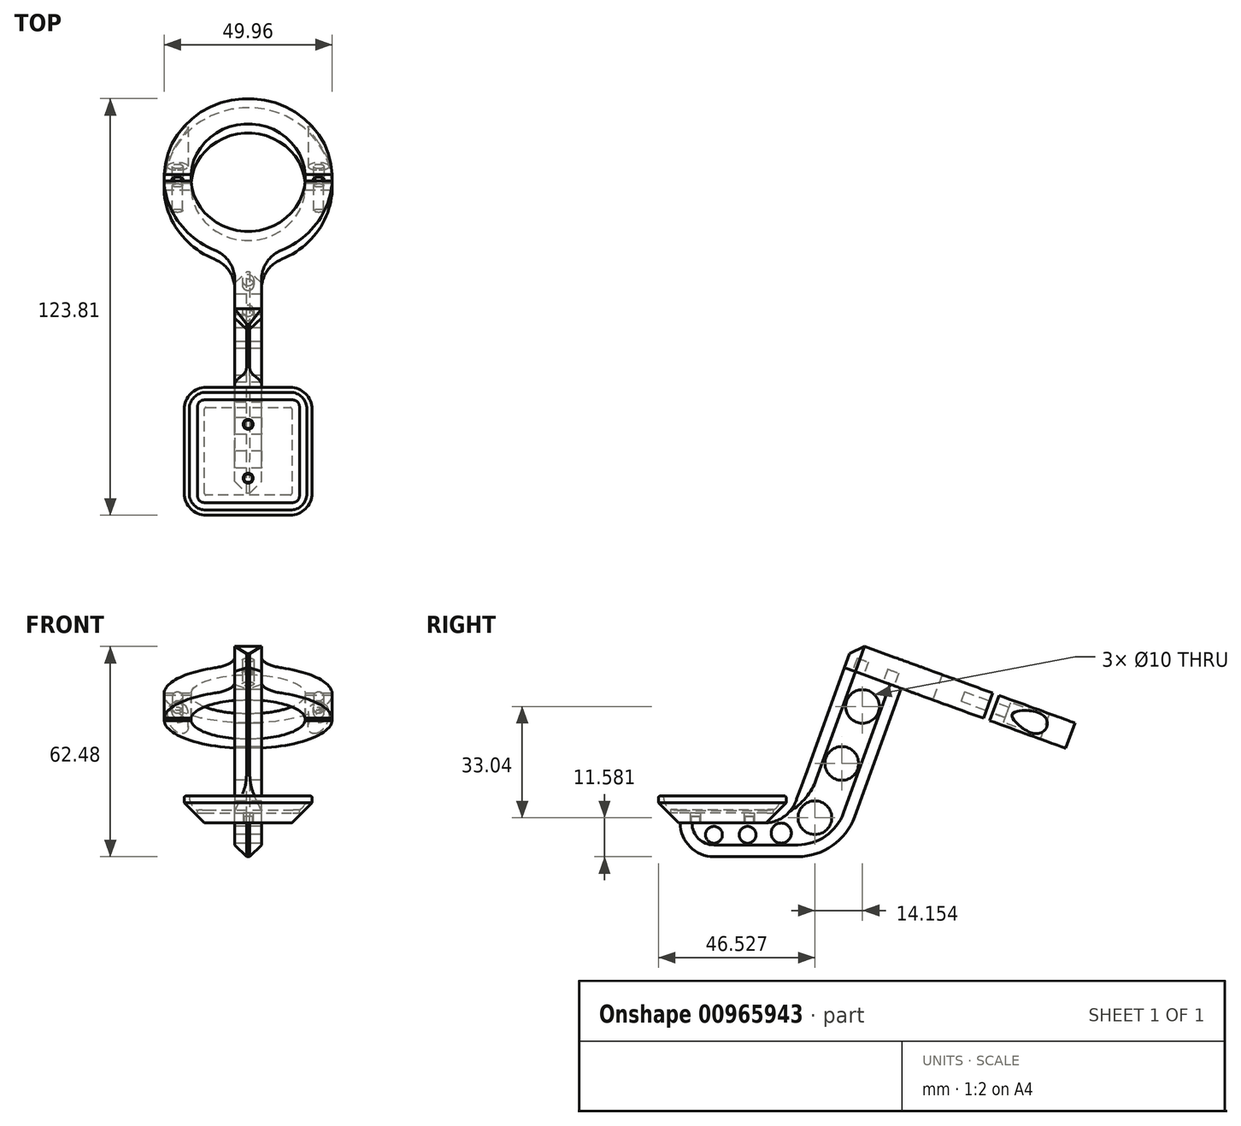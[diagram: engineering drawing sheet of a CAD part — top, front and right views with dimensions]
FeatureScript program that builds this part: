
annotation { "Feature Type Name" : "Feature", "Feature Type Description" : "" }
export const myFeature = defineFeature(function(context is Context, id is Id, definition is map)
    precondition{}
    {
        {
            var Q0;
            Q0=qCreatedBy(makeId("Top.planeOp"),FACE);
            var sketch = newSketch(context, id + "F0", { "sketchPlane" : qUnion([Q0])});
            skLineSegment(sketch, "E0.bottom", {"start": v(-19, 19) * mm, "end": v(19, 19) * mm});
            skLineSegment(sketch, "E0.top", {"start": v(-19, -19) * mm, "end": v(19, -19) * mm});
            skLineSegment(sketch, "E0.left", {"start": v(-19, 19) * mm, "end": v(-19, -19) * mm});
            skLineSegment(sketch, "E0.right", {"start": v(19, 19) * mm, "end": v(19, -19) * mm});
            skSolve(sketch);
        }
        {
            var Q0;
            Q0 = qSketchRegion(id + "F0", true);
            extrude(context, id + "F1", {"entities" : qUnion([Q0]), "depth" : 8 * mm, "offsetDistance" : 25 * mm});
        }
        {
            var Q0;
            Q0=makeQuery(id+"F1.opExtrude","SWEPT_EDGE",EDGE,{"disambiguationData":[OSD([sQuery(id+"F0.wireOp",EDGE,"E0.top"),sQuery(id+"F0.wireOp",EDGE,"E0.left")])]});
            var Q1;
            Q1=makeQuery(id+"F1.opExtrude","SWEPT_EDGE",EDGE,{"disambiguationData":[OSD([sQuery(id+"F0.wireOp",EDGE,"E0.top"),sQuery(id+"F0.wireOp",EDGE,"E0.right")])]});
            var Q2;
            Q2=makeQuery(id+"F1.opExtrude","SWEPT_EDGE",EDGE,{"disambiguationData":[OSD([sQuery(id+"F0.wireOp",EDGE,"E0.bottom"),sQuery(id+"F0.wireOp",EDGE,"E0.right")])]});
            var Q3;
            Q3=makeQuery(id+"F1.opExtrude","SWEPT_EDGE",EDGE,{"disambiguationData":[OSD([sQuery(id+"F0.wireOp",EDGE,"E0.bottom"),sQuery(id+"F0.wireOp",EDGE,"E0.left")])]});
            fillet(context, id + "F2", {"entities" : qUnion([Q0, Q1, Q2, Q3]), "radius" : 6.5 * mm, "tangentPropagation" : true, "allowEdgeOverflow" : false});
        }
        {
            var Q0;
            Q0=makeQuery(id+"F1.opExtrude","CAP_FACE",FACE,{"disambiguationData":[OSD([sQuery(id+"F0.wireOp",EDGE,"E0.bottom"),sQuery(id+"F0.wireOp",EDGE,"E0.top"),sQuery(id+"F0.wireOp",EDGE,"E0.left"),sQuery(id+"F0.wireOp",EDGE,"E0.right")])],"isStart":false});
            var sketch = newSketch(context, id + "F3", { "sketchPlane" : qUnion([Q0])});
            skLineSegment(sketch, "E1.bottom", {"start": v(-17.5, 17.5) * mm, "end": v(17.5, 17.5) * mm});
            skLineSegment(sketch, "E1.top", {"start": v(-17.5, -17.5) * mm, "end": v(17.5, -17.5) * mm});
            skLineSegment(sketch, "E1.left", {"start": v(-17.5, 17.5) * mm, "end": v(-17.5, -17.5) * mm});
            skLineSegment(sketch, "E1.right", {"start": v(17.5, 17.5) * mm, "end": v(17.5, -17.5) * mm});
            skSolve(sketch);
        }
        {
            var Q0;
            Q0 = qSketchRegion(id + "F3", true);
            extrude(context, id + "F4", {"entities" : qUnion([Q0]), "oppositeDirection" : true, "depth" : 5 * mm, "offsetDistance" : 25 * mm});
        }
        {
            var Q0;
            Q0=makeQuery(id+"F4.opExtrude","SWEPT_EDGE",EDGE,{"disambiguationData":[OSD([sQuery(id+"F3.wireOp",EDGE,"E1.top"),sQuery(id+"F3.wireOp",EDGE,"E1.left")])]});
            var Q1;
            Q1=makeQuery(id+"F4.opExtrude","SWEPT_EDGE",EDGE,{"disambiguationData":[OSD([sQuery(id+"F3.wireOp",EDGE,"E1.bottom"),sQuery(id+"F3.wireOp",EDGE,"E1.left")])]});
            var Q2;
            Q2=makeQuery(id+"F4.opExtrude","SWEPT_EDGE",EDGE,{"disambiguationData":[OSD([sQuery(id+"F3.wireOp",EDGE,"E1.bottom"),sQuery(id+"F3.wireOp",EDGE,"E1.right")])]});
            var Q3;
            Q3=makeQuery(id+"F4.opExtrude","SWEPT_EDGE",EDGE,{"disambiguationData":[OSD([sQuery(id+"F3.wireOp",EDGE,"E1.top"),sQuery(id+"F3.wireOp",EDGE,"E1.right")])]});
            fillet(context, id + "F5", {"entities" : qUnion([Q0, Q1, Q2, Q3]), "radius" : 5 * mm, "tangentPropagation" : true, "allowEdgeOverflow" : false});
        }
        {
            var Q0;
            Q0=makeQuery(id+"F4.opExtrude","CAP_EDGE",EDGE,{"disambiguationData":[OSD([sQuery(id+"F3.wireOp",EDGE,"E1.right")])],"isStart":false});
            fillet(context, id + "F6", {"entities" : qUnion([Q0]), "radius" : 5 * mm, "tangentPropagation" : true, "allowEdgeOverflow" : false});
        }
        {
            var Q0;
            Q0=makeQuery(id+"F4.opExtrude","SWEPT_BODY",BODY,{"disambiguationData":[OSD([sQuery(id+"F3.wireOp",EDGE,"E1.bottom"),sQuery(id+"F3.wireOp",EDGE,"E1.top"),sQuery(id+"F3.wireOp",EDGE,"E1.left"),sQuery(id+"F3.wireOp",EDGE,"E1.right")])]});
            var Q1;
            Q1=makeQuery(id+"F1.opExtrude","SWEPT_BODY",BODY,{"disambiguationData":[OSD([sQuery(id+"F0.wireOp",EDGE,"E0.bottom"),sQuery(id+"F0.wireOp",EDGE,"E0.top"),sQuery(id+"F0.wireOp",EDGE,"E0.left"),sQuery(id+"F0.wireOp",EDGE,"E0.right")])]});
            booleanBodies(context, id + "F7", {"operationType" : BooleanOperationType.SUBTRACTION, "tools" : qUnion([Q0]), "targets" : qUnion([Q1])});
        }
        {
            var Q0;
            Q0=makeQuery(id+"F1.opExtrude","CAP_FACE",FACE,{"disambiguationData":[OSD([sQuery(id+"F0.wireOp",EDGE,"E0.bottom"),sQuery(id+"F0.wireOp",EDGE,"E0.top"),sQuery(id+"F0.wireOp",EDGE,"E0.left"),sQuery(id+"F0.wireOp",EDGE,"E0.right")])],"isStart":false});
            var sketch = newSketch(context, id + "F8", { "sketchPlane" : qUnion([Q0])});
            skLineSegment(sketch, "E2.bottom", {"start": v(-15.05, 15.25) * mm, "end": v(15.25, 15.25) * mm});
            skLineSegment(sketch, "E2.top", {"start": v(-15.05, -15.25) * mm, "end": v(15.25, -15.25) * mm});
            skLineSegment(sketch, "E2.left", {"start": v(-15.05, 15.25) * mm, "end": v(-15.05, -15.25) * mm});
            skLineSegment(sketch, "E2.right", {"start": v(15.25, 15.25) * mm, "end": v(15.25, -15.25) * mm});
            skSolve(sketch);
        }
        {
            var Q0;
            Q0 = qSketchRegion(id + "F8", true);
            extrude(context, id + "F9", {"entities" : qUnion([Q0]), "oppositeDirection" : true, "depth" : 5 * mm, "offsetDistance" : 25 * mm});
        }
        {
            var Q0;
            Q0=makeQuery(id+"F1.opExtrude","CAP_EDGE",EDGE,{"disambiguationData":[OSD([sQuery(id+"F0.wireOp",EDGE,"E0.top")])],"isStart":false});
            var Q1;
            {var subQ0=sQuery(id+"F3.wireOp",EDGE,"E1.top");Q1=makeQuery(id+"F7.opBoolean","COPY",EDGE,{"derivedFrom":makeQuery(id+"F6.opFillet","BLEND_EDGE",EDGE,{"blendedFrom":[makeQuery(id+"F4.opExtrude","CAP_EDGE",EDGE,{"disambiguationData":[OSD([subQ0])],"isStart":false}),makeQuery(id+"F4.opExtrude","CAP_FACE",FACE,{"disambiguationData":[OSD([sQuery(id+"F3.wireOp",EDGE,"E1.bottom"),subQ0,sQuery(id+"F3.wireOp",EDGE,"E1.left"),sQuery(id+"F3.wireOp",EDGE,"E1.right")])],"isStart":true})],"blendedInto":[makeQuery(id+"F4.opExtrude","CAP_FACE",FACE,{"disambiguationData":[OSD([sQuery(id+"F3.wireOp",EDGE,"E1.bottom"),subQ0,sQuery(id+"F3.wireOp",EDGE,"E1.left"),sQuery(id+"F3.wireOp",EDGE,"E1.right")])],"isStart":true})]})});}
            fillet(context, id + "F10", {"entities" : qUnion([Q0, Q1]), "radius" : .5 * mm, "tangentPropagation" : true, "allowEdgeOverflow" : false});
        }
        {
            var Q0;
            Q0=qCreatedBy(makeId("Right.planeOp"),FACE);
            var sketch = newSketch(context, id + "F11", { "sketchPlane" : qUnion([Q0])});
            skLineSegment(sketch, "E3", {"start": v(-12.5, 0) * mm, "end": v(12.5, 0) * mm});
            skLineSegment(sketch, "E4", {"start": v(-12.5, 0) * mm, "end": v(-12.5, 0) * mm});
            skLineSegment(sketch, "E5", {"start": v(-2.5, -10) * mm, "end": v(22.41, -10) * mm});
            skLineSegment(sketch, "E6", {"start": v(39.33, 1.84) * mm, "end": v(53.22, 40) * mm});
            skLineSegment(sketch, "E7", {"start": v(21.9, 6.58) * mm, "end": v(36.3, 46.16) * mm});
            skPoint(sketch, "E8.visualSharp", {"position": v(-12.5, -10) * mm});
            skArc(sketch, "E8.filletArc", {"start": v(-12.5, 0) * mm, "mid": v(-9.57, -7.07) * mm, "end": v(-2.5, -10) * mm});
            skArc(sketch, "E9.filletArc", {"start": v(12.5, 0) * mm, "mid": v(18.24, 1.8) * mm, "end": v(21.9, 6.58) * mm});
            skPoint(sketch, "E10.visualSharp", {"position": v(35.02, -10) * mm});
            skArc(sketch, "E10.filletArc", {"start": v(22.41, -10) * mm, "mid": v(32.74, -6.74) * mm, "end": v(39.33, 1.84) * mm});
            skPoint(sketch, "E11.orphan", {"position": v(27.55, 55.87) * mm});
            skLineSegment(sketch, "E12", {"start": v(36.3, 46.16) * mm, "end": v(53.22, 40) * mm});
            skCircle(sketch, "E13", {"center": v(41.68, 34.62) * mm, "radius": 5 * mm});
            skCircle(sketch, "E14", {"center": v(35.52, 17.7) * mm, "radius": 5 * mm});
            skPoint(sketch, "E15.orphan", {"position": v(59, 55.87) * mm});
            skCircle(sketch, "E16", {"center": v(27.53, 1.58) * mm, "radius": 5 * mm});
            skCircle(sketch, "E17", {"center": v(17.53, -3) * mm, "radius": 3 * mm});
            skCircle(sketch, "E18", {"center": v(7.53, -3.5) * mm, "radius": 2.5 * mm});
            skCircle(sketch, "E19", {"center": v(-2.47, -3.5) * mm, "radius": 2.5 * mm});
            skSolve(sketch);
        }
        {
            var Q0;
            Q0 = qSketchRegion(id + "F11", true);
            extrude(context, id + "F12", {"entities" : qUnion([Q0]), "depth" : 4 * mm, "offsetDistance" : 25 * mm, "hasSecondDirection" : true, "secondDirectionOppositeDirection" : true, "secondDirectionDepth" : 4 * mm});
        }
        {
            var Q0;
            Q0=makeQuery(id+"F1.opExtrude","CAP_FACE",FACE,{"disambiguationData":[OSD([sQuery(id+"F0.wireOp",EDGE,"E0.bottom"),sQuery(id+"F0.wireOp",EDGE,"E0.top"),sQuery(id+"F0.wireOp",EDGE,"E0.left"),sQuery(id+"F0.wireOp",EDGE,"E0.right")])],"isStart":true});
            var sketch = newSketch(context, id + "F13", { "sketchPlane" : qUnion([Q0])});
            skCircle(sketch, "E20", {"center": v(0, 8) * mm, "radius": 1.5 * mm});
            skCircle(sketch, "E21", {"center": v(0, -8) * mm, "radius": 1.5 * mm});
            skSolve(sketch);
        }
        {
            var Q0;
            Q0 = qSketchRegion(id + "F13", true);
            extrude(context, id + "F14", {"entities" : qUnion([Q0]), "operationType" : NewBodyOperationType.REMOVE, "oppositeDirection" : true, "depth" : 25 * mm, "offsetDistance" : 25 * mm});
        }
        {
            var Q0;
            Q0=makeQuery(id+"F12.opExtrude","SWEPT_FACE",FACE,{"disambiguationData":[OSD([sQuery(id+"F11.wireOp",EDGE,"E3")])]});
            var sketch = newSketch(context, id + "F15", { "sketchPlane" : qUnion([Q0])});
            skCircle(sketch, "E22", {"center": v(0, 8) * mm, "radius": 1.25 * mm});
            skCircle(sketch, "E23", {"center": v(0, -8) * mm, "radius": 1.25 * mm});
            skPoint(sketch, "E23.centerSnap0", {"position": v(0, -12.5) * mm});
            skSolve(sketch);
        }
        {
            var Q0;
            Q0 = qSketchRegion(id + "F15", true);
            extrude(context, id + "F16", {"entities" : qUnion([Q0]), "operationType" : NewBodyOperationType.ADD, "depth" : 2 * mm, "offsetDistance" : 25 * mm});
        }
        {
            var Q0;
            Q0=makeQuery(id+"F12.opExtrude","SWEPT_FACE",FACE,{"disambiguationData":[OSD([sQuery(id+"F11.wireOp",EDGE,"E12")])]});
            var sketch = newSketch(context, id + "F17", { "sketchPlane" : qUnion([Q0])});
            skLineSegment(sketch, "E24", {"start": v(12, 26.33) * mm, "end": v(4, 26.33) * mm});
            skLineSegment(sketch, "E25", {"start": v(4, 26.33) * mm, "end": v(4, 18.33) * mm});
            skLineSegment(sketch, "E26", {"start": v(4, 18.33) * mm, "end": v(-4, 18.33) * mm});
            skLineSegment(sketch, "E27", {"start": v(-4, 18.33) * mm, "end": v(-4, 26.33) * mm});
            skLineSegment(sketch, "E28", {"start": v(-4, 26.33) * mm, "end": v(-12, 26.33) * mm});
            skLineSegment(sketch, "E29", {"start": v(-12, 26.33) * mm, "end": v(-12, 1.33) * mm});
            skLineSegment(sketch, "E30", {"start": v(-12, 1.33) * mm, "end": v(12, 1.33) * mm});
            skLineSegment(sketch, "E31", {"start": v(12, 1.33) * mm, "end": v(12, 26.33) * mm});
            skSolve(sketch);
        }
        {
            var Q0;
            Q0 = qSketchRegion(id + "F17", true);
            extrude(context, id + "F18", {"entities" : qUnion([Q0]), "oppositeDirection" : true, "depth" : 49 * mm, "offsetDistance" : 25 * mm});
        }
        {
            var Q0;
            Q0=makeQuery(id+"F18.opExtrude","CAP_EDGE",EDGE,{"disambiguationData":[OSD([sQuery(id+"F17.wireOp",EDGE,"E26")])],"isStart":false});
            fillet(context, id + "F19", {"entities" : qUnion([Q0]), "radius" : 15 * mm, "tangentPropagation" : true, "allowEdgeOverflow" : false});
        }
        {
            var Q0;
            Q0=makeQuery(id+"F12.opExtrude","SWEPT_FACE",FACE,{"disambiguationData":[OSD([sQuery(id+"F11.wireOp",EDGE,"E12")])]});
            var sketch = newSketch(context, id + "F20", { "sketchPlane" : qUnion([Q0])});
            skCircle(sketch, "E32", {"center": v(0, 22.67) * mm, "radius": 1.5 * mm});
            skCircle(sketch, "E33", {"center": v(0, 32.33) * mm, "radius": 1.5 * mm});
            skSolve(sketch);
        }
        {
            var Q0;
            Q0 = qSketchRegion(id + "F20", true);
            extrude(context, id + "F21", {"entities" : qUnion([Q0]), "operationType" : NewBodyOperationType.ADD, "depth" : 1.7 * mm, "offsetDistance" : 25 * mm});
        }
        {
            var Q0;
            Q0=makeQuery(id+"F9.opExtrude","SWEPT_EDGE",EDGE,{"disambiguationData":[OSD([sQuery(id+"F8.wireOp",EDGE,"E2.top"),sQuery(id+"F8.wireOp",EDGE,"E2.right")])]});
            var Q1;
            Q1=makeQuery(id+"F9.opExtrude","SWEPT_EDGE",EDGE,{"disambiguationData":[OSD([sQuery(id+"F8.wireOp",EDGE,"E2.bottom"),sQuery(id+"F8.wireOp",EDGE,"E2.right")])]});
            var Q2;
            Q2=makeQuery(id+"F9.opExtrude","SWEPT_EDGE",EDGE,{"disambiguationData":[OSD([sQuery(id+"F8.wireOp",EDGE,"E2.top"),sQuery(id+"F8.wireOp",EDGE,"E2.left")])]});
            var Q3;
            Q3=makeQuery(id+"F9.opExtrude","SWEPT_EDGE",EDGE,{"disambiguationData":[OSD([sQuery(id+"F8.wireOp",EDGE,"E2.bottom"),sQuery(id+"F8.wireOp",EDGE,"E2.left")])]});
            fillet(context, id + "F22", {"entities" : qUnion([Q0, Q1, Q2, Q3]), "radius" : 2 * mm, "tangentPropagation" : true, "allowEdgeOverflow" : false});
        }
        {
            var Q0;
            Q0=makeQuery(id+"F9.opExtrude","SWEPT_BODY",BODY,{"disambiguationData":[OSD([sQuery(id+"F8.wireOp",EDGE,"E2.bottom"),sQuery(id+"F8.wireOp",EDGE,"E2.top"),sQuery(id+"F8.wireOp",EDGE,"E2.left"),sQuery(id+"F8.wireOp",EDGE,"E2.right")])]});
            var Q1;
            Q1=makeQuery(id+"F1.opExtrude","SWEPT_BODY",BODY,{"disambiguationData":[OSD([sQuery(id+"F0.wireOp",EDGE,"E0.bottom"),sQuery(id+"F0.wireOp",EDGE,"E0.top"),sQuery(id+"F0.wireOp",EDGE,"E0.left"),sQuery(id+"F0.wireOp",EDGE,"E0.right")])]});
            booleanBodies(context, id + "F23", {"operationType" : BooleanOperationType.SUBTRACTION, "tools" : qUnion([Q0]), "targets" : qUnion([Q1])});
        }
        {
            var Q0;
            Q0=makeQuery(id+"F1.opExtrude","CAP_EDGE",EDGE,{"disambiguationData":[OSD([sQuery(id+"F0.wireOp",EDGE,"E0.top")])],"isStart":true});
            chamfer(context, id + "F24", {"entities" : qUnion([Q0]), "width" : 6 * mm, "tangentPropagation" : true});
        }
        {
            var Q0;
            Q0=makeQuery(id+"F18.opExtrude","SWEPT_EDGE",EDGE,{"disambiguationData":[OSD([sQuery(id+"F17.wireOp",EDGE,"E25"),sQuery(id+"F17.wireOp",EDGE,"E26")])]});
            chamfer(context, id + "F25", {"entities" : qUnion([Q0]), "width" : 3.5 * mm, "tangentPropagation" : true});
        }
        {
            var Q0;
            Q0=makeQuery(id+"F18.opExtrude","SWEPT_EDGE",EDGE,{"disambiguationData":[OSD([sQuery(id+"F17.wireOp",EDGE,"E26"),sQuery(id+"F17.wireOp",EDGE,"E27")])]});
            var Q1;
            Q1=makeQuery(id+"F19.opFillet","BLEND_EDGE",EDGE,{"blendedFrom":[makeQuery(id+"F18.opExtrude","CAP_EDGE",EDGE,{"disambiguationData":[OSD([sQuery(id+"F17.wireOp",EDGE,"E26")])],"isStart":false}),makeQuery(id+"F18.opExtrude","SWEPT_FACE",FACE,{"disambiguationData":[OSD([sQuery(id+"F17.wireOp",EDGE,"E27")])]})],"blendedInto":[makeQuery(id+"F18.opExtrude","SWEPT_FACE",FACE,{"disambiguationData":[OSD([sQuery(id+"F17.wireOp",EDGE,"E27")])]})]});
            chamfer(context, id + "F26", {"entities" : qUnion([Q0, Q1]), "width" : 3.5 * mm, "tangentPropagation" : true});
        }
        {
            var Q0;
            Q0=makeQuery(id+"F18.opExtrude","SWEPT_BODY",BODY,{"disambiguationData":[OSD([sQuery(id+"F17.wireOp",EDGE,"E24"),sQuery(id+"F17.wireOp",EDGE,"E25"),sQuery(id+"F17.wireOp",EDGE,"E26"),sQuery(id+"F17.wireOp",EDGE,"E27"),sQuery(id+"F17.wireOp",EDGE,"E28"),sQuery(id+"F17.wireOp",EDGE,"E29"),sQuery(id+"F17.wireOp",EDGE,"E30"),sQuery(id+"F17.wireOp",EDGE,"E31")])]});
            var Q1;
            Q1=makeQuery(id+"F12.opExtrude","SWEPT_BODY",BODY,{"disambiguationData":[OSD([sQuery(id+"F11.wireOp",EDGE,"E3"),sQuery(id+"F11.wireOp",EDGE,"E5"),sQuery(id+"F11.wireOp",EDGE,"E6"),sQuery(id+"F11.wireOp",EDGE,"E7"),sQuery(id+"F11.wireOp",EDGE,"E8.filletArc"),sQuery(id+"F11.wireOp",EDGE,"E9.filletArc"),sQuery(id+"F11.wireOp",EDGE,"E10.filletArc"),sQuery(id+"F11.wireOp",EDGE,"E12"),sQuery(id+"F11.wireOp",EDGE,"E13"),sQuery(id+"F11.wireOp",EDGE,"E14"),sQuery(id+"F11.wireOp",EDGE,"E16"),sQuery(id+"F11.wireOp",EDGE,"E17"),sQuery(id+"F11.wireOp",EDGE,"E18"),sQuery(id+"F11.wireOp",EDGE,"E19")])]});
            booleanBodies(context, id + "F27", {"operationType" : BooleanOperationType.SUBTRACTION, "tools" : qUnion([Q0]), "targets" : qUnion([Q1])});
        }
        {
            var Q0;
            Q0=makeQuery(id+"F12.opExtrude","CAP_EDGE",EDGE,{"disambiguationData":[OSD([sQuery(id+"F11.wireOp",EDGE,"E8.filletArc")])],"isStart":false});
            chamfer(context, id + "F28", {"entities" : qUnion([Q0]), "width" : 3.5 * mm, "tangentPropagation" : true});
        }
        {
            var Q0;
            Q0=makeQuery(id+"F12.opExtrude","CAP_EDGE",EDGE,{"disambiguationData":[OSD([sQuery(id+"F11.wireOp",EDGE,"E5")])],"isStart":true});
            chamfer(context, id + "F29", {"entities" : qUnion([Q0]), "width" : 3.5 * mm, "tangentPropagation" : true});
        }
        {
            var Q0;
            Q0=makeQuery(id+"F12.opExtrude","SWEPT_FACE",FACE,{"disambiguationData":[OSD([sQuery(id+"F11.wireOp",EDGE,"E12")])]});
            var sketch = newSketch(context, id + "F30", { "sketchPlane" : qUnion([Q0])});
            skArc(sketch, "E34", {"start": v(-16.97, 62.32) * mm, "mid": v(0, 46.32) * mm, "end": v(16.97, 62.32) * mm});
            skArc(sketch, "E35", {"start": v(-24.98, 62.32) * mm, "mid": v(-20.64, 49.21) * mm, "end": v(-10, 40.4) * mm});
            skLineSegment(sketch, "E36", {"start": v(-24.98, 62.32) * mm, "end": v(-16.97, 62.32) * mm});
            skLineSegment(sketch, "E37", {"start": v(16.97, 62.32) * mm, "end": v(24.98, 62.32) * mm});
            skLineSegment(sketch, "E38", {"start": v(4, 21.83) * mm, "end": v(4, 31.24) * mm});
            skLineSegment(sketch, "E39", {"start": v(-4, 21.83) * mm, "end": v(-4, 31.24) * mm});
            skLineSegment(sketch, "E40", {"start": v(4, 21.83) * mm, "end": v(0.5, 18.33) * mm});
            skLineSegment(sketch, "E41", {"start": v(0.5, 18.33) * mm, "end": v(-0.5, 18.33) * mm});
            skLineSegment(sketch, "E42", {"start": v(-0.5, 18.33) * mm, "end": v(-4, 21.83) * mm});
            skArc(sketch, "E43.trimOffspring", {"start": v(10, 40.4) * mm, "mid": v(20.64, 49.21) * mm, "end": v(24.98, 62.32) * mm});
            skArc(sketch, "E44.filletArc", {"start": v(-4, 31.24) * mm, "mid": v(-5.63, 36.72) * mm, "end": v(-10, 40.4) * mm});
            skArc(sketch, "E45.filletArc", {"start": v(10, 40.4) * mm, "mid": v(5.63, 36.72) * mm, "end": v(4, 31.24) * mm});
            skSolve(sketch);
        }
        {
            var Q0;
            Q0 = qSketchRegion(id + "F30", true);
            extrude(context, id + "F31", {"entities" : qUnion([Q0]), "depth" : 8 * mm, "offsetDistance" : 25 * mm});
        }
        {
            var Q0;
            Q0=makeQuery(id+"F31.opExtrude","CAP_EDGE",EDGE,{"disambiguationData":[OSD([sQuery(id+"F30.wireOp",EDGE,"E41")])],"isStart":false});
            chamfer(context, id + "F32", {"entities" : qUnion([Q0]), "width" : 3.5 * mm, "tangentPropagation" : true});
        }
        {
            var Q0;
            Q0=makeQuery(id+"F12.opExtrude","SWEPT_FACE",FACE,{"disambiguationData":[OSD([sQuery(id+"F11.wireOp",EDGE,"E12")])]});
            var sketch = newSketch(context, id + "F33", { "sketchPlane" : qUnion([Q0])});
            skCircle(sketch, "E46", {"center": v(0, 22.67) * mm, "radius": 1.75 * mm});
            skCircle(sketch, "E47", {"center": v(0, 32.33) * mm, "radius": 1.75 * mm});
            skSolve(sketch);
        }
        {
            var Q0;
            Q0 = qSketchRegion(id + "F33", true);
            extrude(context, id + "F34", {"entities" : qUnion([Q0]), "operationType" : NewBodyOperationType.REMOVE, "depth" : 4 * mm, "offsetDistance" : 25 * mm});
        }
        {
            var Q0;
            Q0=makeQuery(id+"F31.opExtrude","SWEPT_FACE",FACE,{"disambiguationData":[OSD([sQuery(id+"F30.wireOp",EDGE,"E36")])]});
            var sketch = newSketch(context, id + "F35", { "sketchPlane" : qUnion([Q0])});
            skCircle(sketch, "E48", {"center": v(20.98, 59.79) * mm, "radius": 1.5 * mm});
            skCircle(sketch, "E49", {"center": v(-20.98, 59.79) * mm, "radius": 1.5 * mm});
            skSolve(sketch);
        }
        {
            var Q0;
            Q0 = qSketchRegion(id + "F35", true);
            extrude(context, id + "F36", {"entities" : qUnion([Q0]), "operationType" : NewBodyOperationType.REMOVE, "oppositeDirection" : true, "depth" : 8 * mm, "offsetDistance" : 25 * mm});
        }
        {
            var Q0;
            Q0=makeQuery(id+"F31.opExtrude","CAP_FACE",FACE,{"disambiguationData":[OSD([sQuery(id+"F30.wireOp",EDGE,"E34"),sQuery(id+"F30.wireOp",EDGE,"E35"),sQuery(id+"F30.wireOp",EDGE,"E36"),sQuery(id+"F30.wireOp",EDGE,"E37"),sQuery(id+"F30.wireOp",EDGE,"E38"),sQuery(id+"F30.wireOp",EDGE,"E39"),sQuery(id+"F30.wireOp",EDGE,"E40"),sQuery(id+"F30.wireOp",EDGE,"E41"),sQuery(id+"F30.wireOp",EDGE,"E42"),sQuery(id+"F30.wireOp",EDGE,"E43.trimOffspring"),sQuery(id+"F30.wireOp",EDGE,"E44.filletArc"),sQuery(id+"F30.wireOp",EDGE,"E45.filletArc")])],"isStart":false});
            var sketch = newSketch(context, id + "F37", { "sketchPlane" : qUnion([Q0])});
            skArc(sketch, "E50", {"start": v(16.97, 64.32) * mm, "mid": v(0, 80.32) * mm, "end": v(-16.97, 64.32) * mm});
            skLineSegment(sketch, "E51", {"start": v(24.98, 64.32) * mm, "end": v(16.97, 64.32) * mm});
            skArc(sketch, "E52", {"start": v(24.98, 64.32) * mm, "mid": v(0, 88.32) * mm, "end": v(-24.98, 64.32) * mm});
            skLineSegment(sketch, "E53.trimOffspring", {"start": v(-16.97, 64.32) * mm, "end": v(-24.98, 64.32) * mm});
            skSolve(sketch);
        }
        {
            var Q0;
            Q0 = qSketchRegion(id + "F37", true);
            extrude(context, id + "F38", {"entities" : qUnion([Q0]), "oppositeDirection" : true, "depth" : 8 * mm, "offsetDistance" : 25 * mm});
        }
        {
            var Q0;
            Q0=makeQuery(id+"F38.opExtrude","SWEPT_FACE",FACE,{"disambiguationData":[OSD([sQuery(id+"F37.wireOp",EDGE,"E51")])]});
            var sketch = newSketch(context, id + "F39", { "sketchPlane" : qUnion([Q0])});
            skCircle(sketch, "E54", {"center": v(20.97, 59.79) * mm, "radius": 1.63 * mm});
            skCircle(sketch, "E55", {"center": v(-20.97, 59.79) * mm, "radius": 1.65 * mm});
            skSolve(sketch);
        }
        {
            var Q0;
            Q0 = qSketchRegion(id + "F39", true);
            extrude(context, id + "F40", {"entities" : qUnion([Q0]), "operationType" : NewBodyOperationType.REMOVE, "oppositeDirection" : true, "depth" : 25 * mm, "offsetDistance" : 25 * mm});
        }
        {
            var Q0;
            Q0=makeQuery(id+"F38.opExtrude","SWEPT_FACE",FACE,{"disambiguationData":[OSD([sQuery(id+"F37.wireOp",EDGE,"E51")])]});
            var sketch = newSketch(context, id + "F41", { "sketchPlane" : qUnion([Q0])});
            skCircle(sketch, "E56", {"center": v(20.97, 59.79) * mm, "radius": 3.15 * mm});
            skCircle(sketch, "E57", {"center": v(-20.97, 59.79) * mm, "radius": 3.15 * mm});
            skSolve(sketch);
        }
        {
            var Q0;
            Q0 = qSketchRegion(id + "F41", true);
            extrude(context, id + "F42", {"entities" : qUnion([Q0]), "operationType" : NewBodyOperationType.REMOVE, "oppositeDirection" : true, "depth" : 25 * mm, "offsetDistance" : 25 * mm, "hasSecondDirection" : true, "secondDirectionOppositeDirection" : true, "secondDirectionDepth" : 4 * mm});
        }
    });
